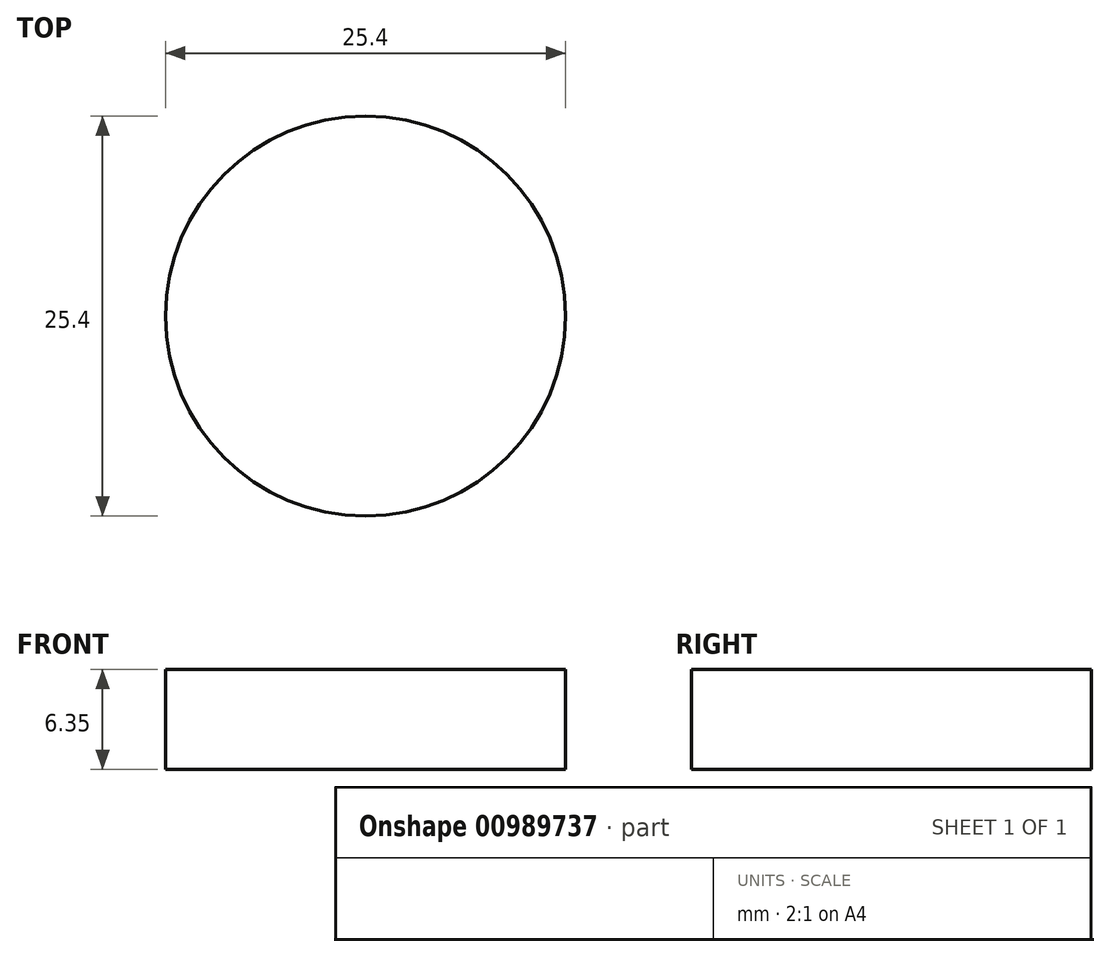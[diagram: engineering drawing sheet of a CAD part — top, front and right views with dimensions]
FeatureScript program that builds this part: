
annotation { "Feature Type Name" : "Feature", "Feature Type Description" : "" }
export const myFeature = defineFeature(function(context is Context, id is Id, definition is map)
    precondition{}
    {
        {
            var Q0;
            Q0=qCreatedBy(makeId("Top.planeOp"),FACE);
            var sketch = newSketch(context, id + "F0", { "sketchPlane" : qUnion([Q0])});
            skCircle(sketch, "E0", {"center": v(0, 0) * mm, "radius": 12.7 * mm});
            skSolve(sketch);
        }
        {
            var Q0;
            Q0=sQuery(id+"F0.wireOp",EDGE,"E0");
            extrude(context, id + "F1", {"bodyType" : ToolBodyType.SURFACE, "surfaceEntities" : qUnion([Q0]), "depth" : 6.35 * mm, "offsetDistance" : 25.4 * mm});
        }
        {
            var Q0;
            Q0=makeQuery(id+"F1.opExtrude","CAP_EDGE",EDGE,{"disambiguationData":[OSD([sQuery(id+"F0.wireOp",EDGE,"E0")])],"isStart":true});
            var Q1;
            Q1=makeQuery(id+"F1.opExtrude","CAP_EDGE",EDGE,{"disambiguationData":[OSD([sQuery(id+"F0.wireOp",EDGE,"E0")])],"isStart":false});
            loft(context, id + "F2", {"bodyType" : ToolBodyType.SURFACE, "surfaceOperationType" : NewSurfaceOperationType.ADD, "wireProfilesArray" : [{ "wireProfileEntities" : qUnion([Q0]) }, { "wireProfileEntities" : qUnion([Q1]) }]});
        }
    });
